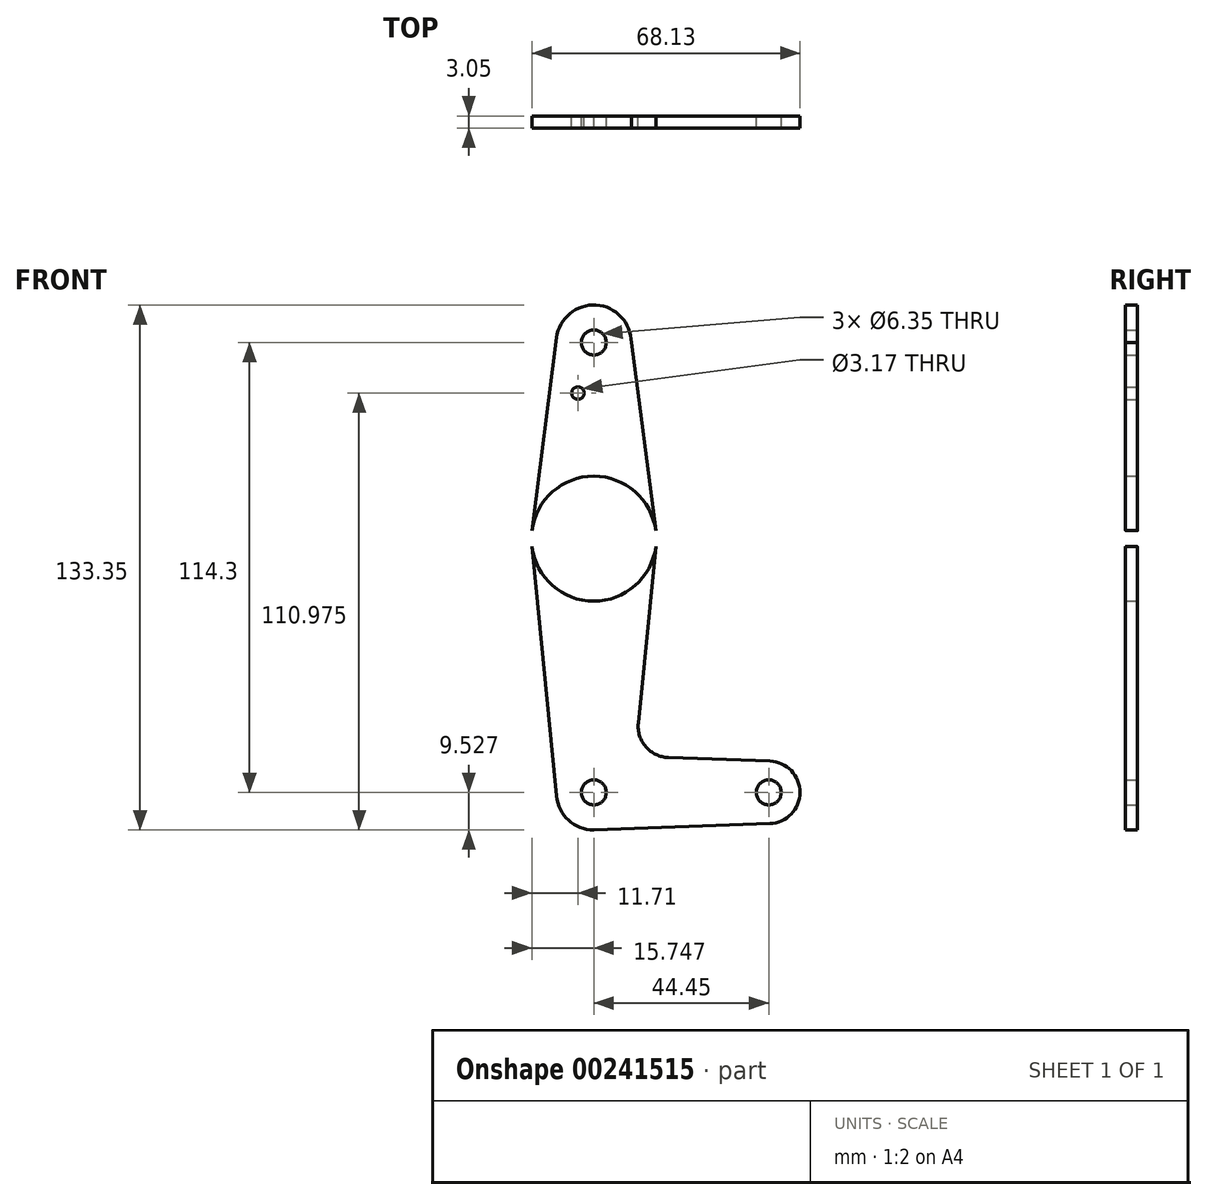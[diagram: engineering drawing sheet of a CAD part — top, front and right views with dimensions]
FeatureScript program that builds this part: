
annotation { "Feature Type Name" : "Feature", "Feature Type Description" : "" }
export const myFeature = defineFeature(function(context is Context, id is Id, definition is map)
    precondition{}
    {
        {
            var Q0;
            Q0=qCreatedBy(makeId("Front.planeOp"),FACE);
            var sketch = newSketch(context, id + "F0", { "sketchPlane" : qUnion([Q0])});
            skCircle(sketch, "E0", {"center": v(10.7, 83.64) * mm, "radius": 9.53 * mm});
            skLineSegment(sketch, "E1", {"start": v(10.7, 83.64) * mm, "end": v(10.7, -30.66) * mm});
            skLineSegment(sketch, "E2", {"start": v(10.7, -30.66) * mm, "end": v(55.15, -30.66) * mm});
            skLineSegment(sketch, "E3", {"start": v(-39.22, -30.66) * mm, "end": v(-39.22, 32.84) * mm});
            skCircle(sketch, "E4", {"center": v(10.7, 33.8) * mm, "radius": 15.88 * mm});
            skCircle(sketch, "E5", {"center": v(10.7, -30.66) * mm, "radius": 9.53 * mm});
            skCircle(sketch, "E6", {"center": v(55.15, -30.66) * mm, "radius": 7.94 * mm});
            skLineSegment(sketch, "E7", {"start": v(-39.22, 32.84) * mm, "end": v(-39.22, 69.36) * mm});
            skCircle(sketch, "E8", {"center": v(6.66, 70.79) * mm, "radius": 1.59 * mm});
            skLineSegment(sketch, "E9", {"start": v(20.22, 83.64) * mm, "end": v(26.44, 35.85) * mm});
            skLineSegment(sketch, "E10", {"start": v(-5.05, 31.79) * mm, "end": v(1.22, -31.6) * mm});
            skLineSegment(sketch, "E11", {"start": v(26.44, 31.75) * mm, "end": v(22, -13.09) * mm});
            skPoint(sketch, "E11.endSnap0", {"position": v(32.92, -30.66) * mm});
            skLineSegment(sketch, "E12", {"start": v(29.63, -21.81) * mm, "end": v(55.43, -22.73) * mm});
            skLineSegment(sketch, "E13", {"start": v(10.7, -40.19) * mm, "end": v(55.43, -38.6) * mm});
            skLineSegment(sketch, "E14", {"start": v(-5.05, 35.81) * mm, "end": v(1.25, 84.85) * mm});
            skPoint(sketch, "E15.newPointA", {"position": v(20.27, -30.66) * mm});
            skPoint(sketch, "E15.newPointB", {"position": v(10.7, -21.14) * mm});
            skArc(sketch, "E15.filletArc", {"start": v(22, -13.09) * mm, "mid": v(23.93, -19.1) * mm, "end": v(29.63, -21.81) * mm});
            skCircle(sketch, "E16", {"center": v(10.7, 83.64) * mm, "radius": 3.18 * mm});
            skCircle(sketch, "E17", {"center": v(10.7, 33.8) * mm, "radius": 3.18 * mm});
            skCircle(sketch, "E18", {"center": v(10.7, -30.66) * mm, "radius": 3.18 * mm});
            skCircle(sketch, "E19", {"center": v(55.15, -30.66) * mm, "radius": 3.18 * mm});
            skSolve(sketch);
        }
        {
            var Q0;
            Q0=makeQuery(id+"F0.imprint","IMPRINT",FACE,{"disambiguationData":[TD([[makeQuery(id+"F0.imprint","IMPRINT",EDGE,{"derivedFrom":sQuery(id+"F0.wireOp",EDGE,"VcafkP6C-iaGr-SdzQ-J9Z3-IknjFXCwmc84")}),-1.0]])]});
            var Q1;
            {var subQ0=sQuery(id+"F0.wireOp",EDGE,"E9");Q1=makeQuery(id+"F0.imprint","IMPRINT",FACE,{"disambiguationData":[TD([[makeQuery(id+"F0.imprint","IMPRINT",EDGE,{"derivedFrom":subQ0}),-1.0]])]});}
            var Q2;
            Q2=makeQuery(id+"F0.imprint","IMPRINT",FACE,{"disambiguationData":[TD([[makeQuery(id+"F0.imprint","IMPRINT",EDGE,{"derivedFrom":sQuery(id+"F0.wireOp",EDGE,"E8")}),-1.0]])]});
            var Q3;
            {var subQ0=sQuery(id+"F0.wireOp",EDGE,"E4");var subQ3=sQuery(id+"F0.wireOp",EDGE,"E1");var subQ4=makeQuery(id+"F0.imprint","INTERSECT",VERTEX,{"disambiguationData":[OD(0.0)],"derivedFrom":[subQ3,subQ0]});Q3=makeQuery(id+"F0.imprint","IMPRINT",FACE,{"disambiguationData":[TD([[makeQuery(id+"F0.imprint","IMPRINT",EDGE,{"disambiguationData":[TD([[subQ4,-1.0]])],"derivedFrom":subQ3}),-1.0]])]});}
            var Q4;
            {var subQ0=sQuery(id+"F0.wireOp",EDGE,"E4");var subQ2=sQuery(id+"F0.wireOp",EDGE,"E1");var subQ5=makeQuery(id+"F0.imprint","INTERSECT",VERTEX,{"disambiguationData":[OD(0.0)],"derivedFrom":[subQ2,subQ0]});Q4=makeQuery(id+"F0.imprint","IMPRINT",FACE,{"disambiguationData":[TD([[makeQuery(id+"F0.imprint","IMPRINT",EDGE,{"disambiguationData":[TD([[subQ5,-1.0]])],"derivedFrom":subQ2}),1.0]])]});}
            var Q5;
            {var subQ0=sQuery(id+"F0.wireOp",EDGE,"E11");Q5=makeQuery(id+"F0.imprint","IMPRINT",FACE,{"disambiguationData":[TD([[makeQuery(id+"F0.imprint","IMPRINT",EDGE,{"derivedFrom":subQ0}),-1.0]])]});}
            var Q6;
            {var subQ5=sQuery(id+"F0.wireOp",EDGE,"E10");Q6=makeQuery(id+"F0.imprint","IMPRINT",FACE,{"disambiguationData":[TD([[makeQuery(id+"F0.imprint","IMPRINT",EDGE,{"derivedFrom":subQ5}),1.0]])]});}
            var Q7;
            {var subQ0=sQuery(id+"F0.wireOp",EDGE,"E6");var subQ1=sQuery(id+"F0.wireOp",EDGE,"E2");var subQ2=makeQuery(id+"F0.imprint","INTERSECT",VERTEX,{"derivedFrom":[subQ1,subQ0]});Q7=makeQuery(id+"F0.imprint","IMPRINT",FACE,{"disambiguationData":[TD([[makeQuery(id+"F0.imprint","IMPRINT",EDGE,{"disambiguationData":[TD([[subQ2,1.0]])],"derivedFrom":subQ1}),-1.0]])]});}
            var Q8;
            {var subQ0=sQuery(id+"F0.wireOp",EDGE,"E5");var subQ4=sQuery(id+"F0.wireOp",EDGE,"E1");var subQ5=makeQuery(id+"F0.imprint","INTERSECT",VERTEX,{"derivedFrom":[subQ4,subQ0]});Q8=makeQuery(id+"F0.imprint","IMPRINT",FACE,{"disambiguationData":[TD([[makeQuery(id+"F0.imprint","IMPRINT",EDGE,{"disambiguationData":[TD([[subQ5,-1.0]])],"derivedFrom":subQ4}),-1.0]])]});}
            var Q9;
            Q9=makeQuery(id+"F0.imprint","IMPRINT",FACE,{"disambiguationData":[TD([[makeQuery(id+"F0.imprint","IMPRINT",EDGE,{"derivedFrom":sQuery(id+"F0.wireOp",EDGE,"ZStTOvhF-xRMX-Z8By-5GSv-39Ld4zUZNWK4")}),-1.0]])]});
            var Q10;
            {var subQ0=sQuery(id+"F0.wireOp",EDGE,"E5");var subQ1=sQuery(id+"F0.wireOp",EDGE,"E1");var subQ2=makeQuery(id+"F0.imprint","INTERSECT",VERTEX,{"derivedFrom":[subQ1,subQ0]});Q10=makeQuery(id+"F0.imprint","IMPRINT",FACE,{"disambiguationData":[TD([[makeQuery(id+"F0.imprint","IMPRINT",EDGE,{"disambiguationData":[TD([[subQ2,-1.0]])],"derivedFrom":subQ1}),1.0]])]});}
            var Q11;
            Q11=makeQuery(id+"F0.imprint","IMPRINT",FACE,{"disambiguationData":[TD([[makeQuery(id+"F0.imprint","IMPRINT",EDGE,{"derivedFrom":sQuery(id+"F0.wireOp",EDGE,"E16")}),-1.0]])]});
            var Q12;
            Q12=makeQuery(id+"F0.imprint","IMPRINT",FACE,{"disambiguationData":[TD([[makeQuery(id+"F0.imprint","IMPRINT",EDGE,{"derivedFrom":sQuery(id+"F0.wireOp",EDGE,"E19")}),-1.0]])]});
            extrude(context, id + "F1", {"entities" : qUnion([Q0, Q1, Q2, Q3, Q4, Q5, Q6, Q7, Q8, Q9, Q10, Q11, Q12]), "depth" : 3.05 * mm});
        }
    });
